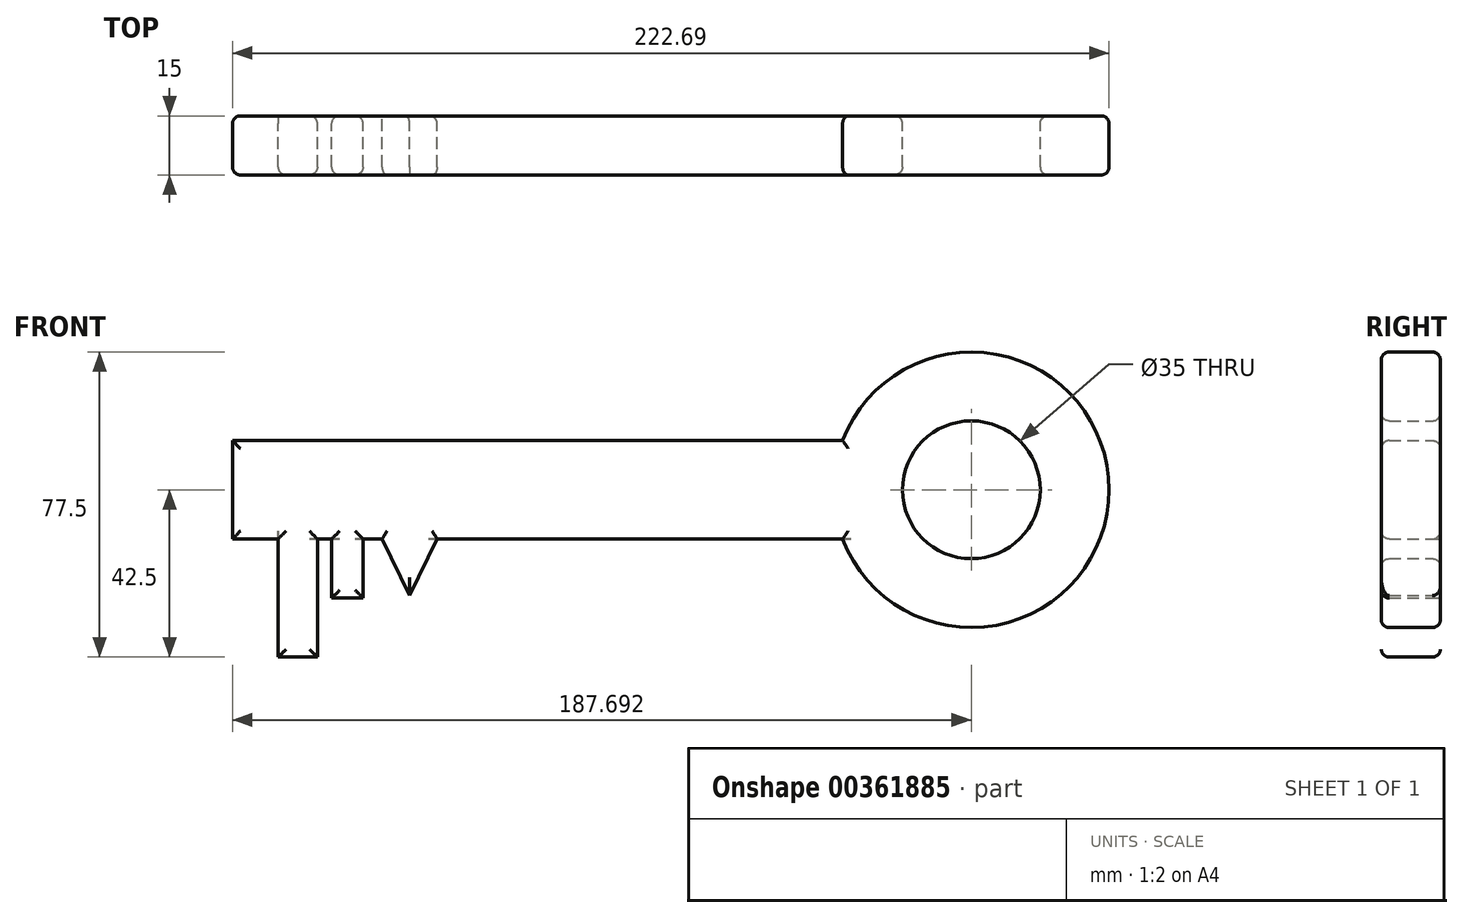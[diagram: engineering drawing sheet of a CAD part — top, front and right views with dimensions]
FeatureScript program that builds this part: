
annotation { "Feature Type Name" : "Feature", "Feature Type Description" : "" }
export const myFeature = defineFeature(function(context is Context, id is Id, definition is map)
    precondition{}
    {
        {
            var Q0;
            Q0=qCreatedBy(makeId("Front.planeOp"),FACE);
            var sketch = newSketch(context, id + "F0", { "sketchPlane" : qUnion([Q0])});
            skLineSegment(sketch, "E0.bottom", {"start": v(-77.5, 12.5) * mm, "end": v(77.5, 12.5) * mm});
            skLineSegment(sketch, "E0.top", {"start": v(-77.5, -12.5) * mm, "end": v(77.5, -12.5) * mm});
            skLineSegment(sketch, "E0.left", {"start": v(-77.5, 12.5) * mm, "end": v(-77.5, -12.5) * mm});
            skLineSegment(sketch, "E0.right", {"start": v(77.5, 12.5) * mm, "end": v(77.5, -12.5) * mm});
            skPoint(sketch, "E0.middle", {"position": v(0, 0) * mm});
            skLineSegment(sketch, "E1.bottom", {"start": v(-65.93, -42.5) * mm, "end": v(-55.93, -42.5) * mm});
            skLineSegment(sketch, "E1.top", {"start": v(-65.93, -12.5) * mm, "end": v(-55.93, -12.5) * mm});
            skLineSegment(sketch, "E1.left", {"start": v(-65.93, -42.5) * mm, "end": v(-65.93, -12.5) * mm});
            skLineSegment(sketch, "E1.right", {"start": v(-55.93, -42.5) * mm, "end": v(-55.93, -12.5) * mm});
            skLineSegment(sketch, "E2.bottom", {"start": v(-52.33, -27.5) * mm, "end": v(-44.33, -27.5) * mm});
            skLineSegment(sketch, "E2.top", {"start": v(-52.33, -12.5) * mm, "end": v(-44.33, -12.5) * mm});
            skLineSegment(sketch, "E2.left", {"start": v(-52.33, -27.5) * mm, "end": v(-52.33, -12.5) * mm});
            skLineSegment(sketch, "E2.right", {"start": v(-44.33, -27.5) * mm, "end": v(-44.33, -12.5) * mm});
            skLineSegment(sketch, "E3", {"start": v(-39.5, -12.5) * mm, "end": v(-32.5, -26.89) * mm});
            skLineSegment(sketch, "E4", {"start": v(-32.5, -26.89) * mm, "end": v(-25.5, -12.5) * mm});
            skLineSegment(sketch, "E5", {"start": v(-32.5, -12.5) * mm, "end": v(-32.5, -26.89) * mm});
            skArc(sketch, "E6", {"start": v(77.5, -12.5) * mm, "mid": v(145.2, 0) * mm, "end": v(77.5, 12.5) * mm});
            skCircle(sketch, "E7", {"center": v(110.2, 0) * mm, "radius": 17.5 * mm});
            skLineSegment(sketch, "E8", {"start": v(-74.04, 0) * mm, "end": v(77.5, 0) * mm, "construction": true});
            skPoint(sketch, "E8.startSnap0", {"position": v(-77.5, 0) * mm});
            skSolve(sketch);
        }
        {
            var Q0;
            Q0=makeQuery(id+"F0.imprint","IMPRINT",FACE,{"disambiguationData":[TD([[makeQuery(id+"F0.imprint","IMPRINT",EDGE,{"derivedFrom":sQuery(id+"F0.wireOp",EDGE,"E0.bottom")}),-1.0]])]});
            var Q1;
            Q1=makeQuery(id+"F0.imprint","IMPRINT",FACE,{"disambiguationData":[TD([[makeQuery(id+"F0.imprint","IMPRINT",EDGE,{"derivedFrom":sQuery(id+"F0.wireOp",EDGE,"E0.right")}),1.0]])]});
            var Q2;
            {var subQ0=sQuery(id+"F0.wireOp",EDGE,"E3");Q2=makeQuery(id+"F0.imprint","IMPRINT",FACE,{"disambiguationData":[TD([[makeQuery(id+"F0.imprint","IMPRINT",EDGE,{"derivedFrom":subQ0}),1.0]])]});}
            var Q3;
            {var subQ0=sQuery(id+"F0.wireOp",EDGE,"E4");Q3=makeQuery(id+"F0.imprint","IMPRINT",FACE,{"disambiguationData":[TD([[makeQuery(id+"F0.imprint","IMPRINT",EDGE,{"derivedFrom":subQ0}),1.0]])]});}
            var Q4;
            Q4=makeQuery(id+"F0.imprint","IMPRINT",FACE,{"disambiguationData":[TD([[makeQuery(id+"F0.imprint","IMPRINT",EDGE,{"derivedFrom":sQuery(id+"F0.wireOp",EDGE,"E2.bottom")}),1.0]])]});
            var Q5;
            Q5=makeQuery(id+"F0.imprint","IMPRINT",FACE,{"disambiguationData":[TD([[makeQuery(id+"F0.imprint","IMPRINT",EDGE,{"derivedFrom":sQuery(id+"F0.wireOp",EDGE,"E1.bottom")}),1.0]])]});
            extrude(context, id + "F1", {"entities" : qUnion([Q0, Q1, Q2, Q3, Q4, Q5]), "depth" : 15 * mm});
        }
        {
            var Q0;
            Q0=makeQuery(id+"F1.opExtrude","CAP_EDGE",EDGE,{"disambiguationData":[OSD([sQuery(id+"F0.wireOp",EDGE,"E0.bottom")])],"isStart":false});
            var Q1;
            Q1=makeQuery(id+"F1.opExtrude","CAP_FACE",FACE,{"disambiguationData":[OSD([sQuery(id+"F0.wireOp",EDGE,"E0.bottom"),sQuery(id+"F0.wireOp",EDGE,"E0.top"),sQuery(id+"F0.wireOp",EDGE,"E0.left"),sQuery(id+"F0.wireOp",EDGE,"E1.bottom"),sQuery(id+"F0.wireOp",EDGE,"E1.left"),sQuery(id+"F0.wireOp",EDGE,"E1.right"),sQuery(id+"F0.wireOp",EDGE,"E2.bottom"),sQuery(id+"F0.wireOp",EDGE,"E2.left"),sQuery(id+"F0.wireOp",EDGE,"E2.right"),sQuery(id+"F0.wireOp",EDGE,"E3"),sQuery(id+"F0.wireOp",EDGE,"E4"),sQuery(id+"F0.wireOp",EDGE,"E6"),sQuery(id+"F0.wireOp",EDGE,"E7")])],"isStart":false});
            var Q2;
            Q2=makeQuery(id+"F1.opExtrude","CAP_EDGE",EDGE,{"disambiguationData":[OSD([sQuery(id+"F0.wireOp",EDGE,"E4")])],"isStart":true});
            var Q3;
            Q3=makeQuery(id+"F1.opExtrude","CAP_EDGE",EDGE,{"disambiguationData":[OSD([sQuery(id+"F0.wireOp",EDGE,"E7")])],"isStart":true});
            var Q4;
            Q4=makeQuery(id+"F1.opExtrude","CAP_EDGE",EDGE,{"disambiguationData":[OSD([sQuery(id+"F0.wireOp",EDGE,"E0.bottom")])],"isStart":true});
            var Q5;
            Q5=makeQuery(id+"F1.opExtrude","CAP_EDGE",EDGE,{"disambiguationData":[OSD([sQuery(id+"F0.wireOp",EDGE,"E0.left")])],"isStart":true});
            var Q6;
            Q6=makeQuery(id+"F1.opExtrude","CAP_EDGE",EDGE,{"disambiguationData":[OSD([sQuery(id+"F0.wireOp",EDGE,"E1.bottom")])],"isStart":true});
            var Q7;
            Q7=makeQuery(id+"F1.opExtrude","CAP_EDGE",EDGE,{"disambiguationData":[OSD([sQuery(id+"F0.wireOp",EDGE,"E1.right")])],"isStart":true});
            var Q8;
            Q8=makeQuery(id+"F1.opExtrude","CAP_EDGE",EDGE,{"disambiguationData":[OSD([sQuery(id+"F0.wireOp",EDGE,"E2.left")])],"isStart":true});
            var Q9;
            Q9=makeQuery(id+"F1.opExtrude","CAP_EDGE",EDGE,{"disambiguationData":[OSD([sQuery(id+"F0.wireOp",EDGE,"E6")])],"isStart":true});
            var Q10;
            Q10=makeQuery(id+"F1.opExtrude","CAP_EDGE",EDGE,{"disambiguationData":[OSD([sQuery(id+"F0.wireOp",EDGE,"E6")])],"isStart":false});
            var Q11;
            Q11=makeQuery(id+"F1.opExtrude","CAP_EDGE",EDGE,{"disambiguationData":[OSD([sQuery(id+"F0.wireOp",EDGE,"E2.right")])],"isStart":true});
            var Q12;
            {var subQ0=sQuery(id+"F0.wireOp",EDGE,"E0.top");Q12=makeQuery(id+"F1.opExtrude","CAP_EDGE",EDGE,{"disambiguationData":[OSD([subQ0]),TDD([makeQuery(id+"F0.imprint","IMPRINT",EDGE,{"disambiguationData":[TD([[makeQuery(id+"F0.imprint","INTERSECT",VERTEX,{"derivedFrom":[subQ0,sQuery(id+"F0.wireOp",EDGE,"E0.left")]}),-1.0]])],"derivedFrom":subQ0})])],"isStart":true});}
            fillet(context, id + "F2", {"entities" : qUnion([Q0, Q1, Q2, Q3, Q4, Q5, Q6, Q7, Q8, Q9, Q10, Q11, Q12]), "radius" : 2 * mm, "tangentPropagation" : true, "allowEdgeOverflow" : false});
        }
    });
